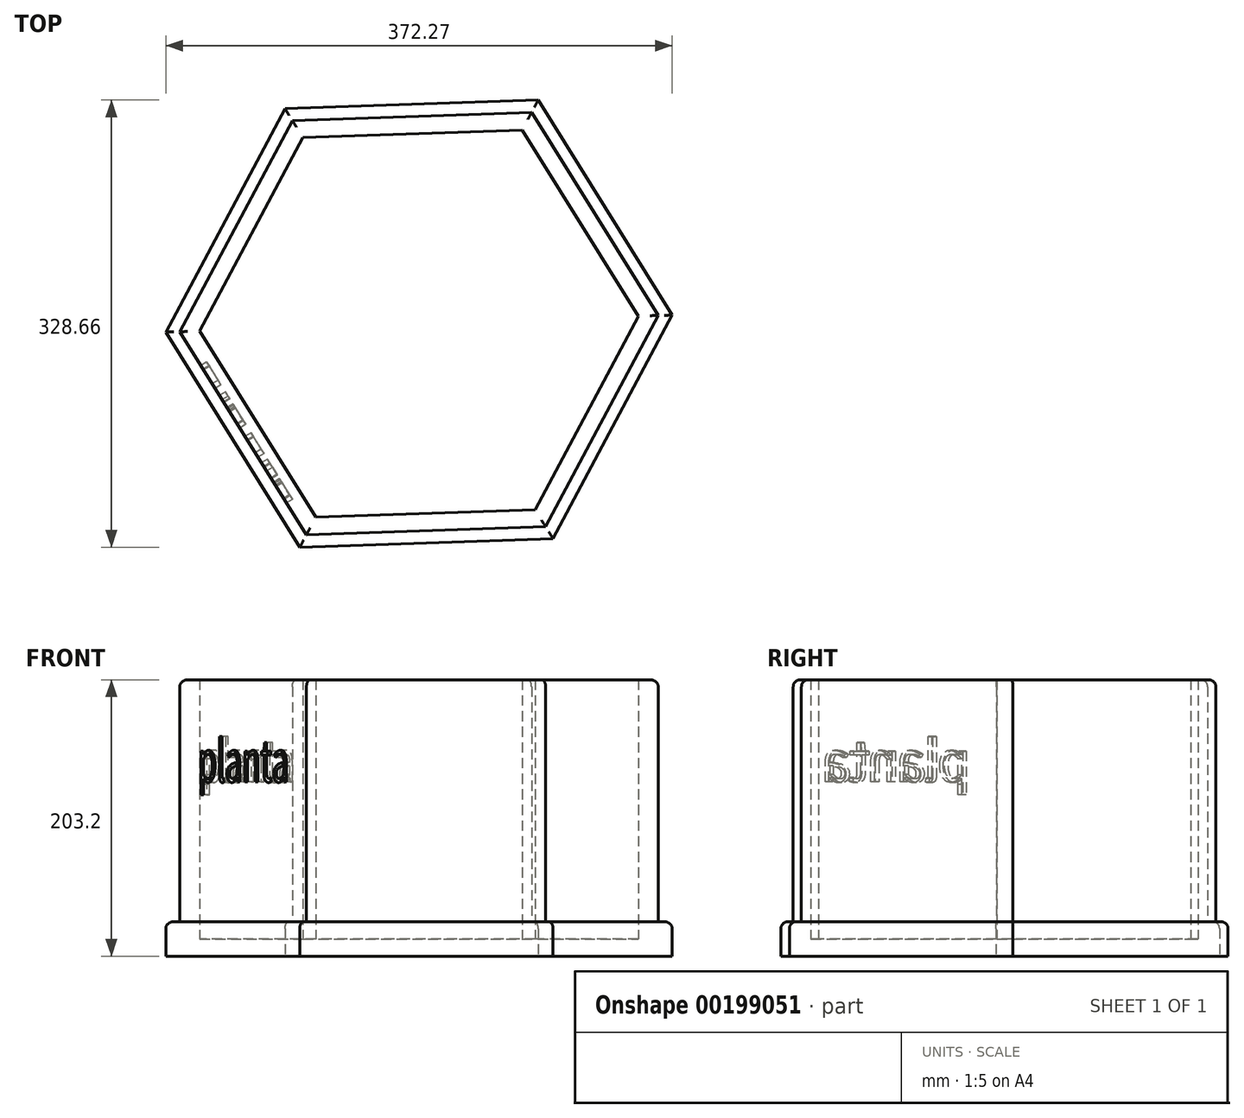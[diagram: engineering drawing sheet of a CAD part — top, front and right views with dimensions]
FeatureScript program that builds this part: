
annotation { "Feature Type Name" : "Feature", "Feature Type Description" : "" }
export const myFeature = defineFeature(function(context is Context, id is Id, definition is map)
    precondition{}
    {
        {
            var Q0;
            Q0=qCreatedBy(makeId("Top.planeOp"),FACE);
            var sketch = newSketch(context, id + "F0", { "sketchPlane" : qUnion([Q0])});
            skCircle(sketch, "E0.cCircle", {"center": v(-49.02, 41.52) * mm, "radius": 152.4 * mm, "construction": true});
            skLineSegment(sketch, "E0.0", {"start": v(126.85, 47.53) * mm, "end": v(44.12, -107.79) * mm});
            skLineSegment(sketch, "E0.1", {"start": v(44.12, -107.79) * mm, "end": v(-131.76, -113.8) * mm});
            skLineSegment(sketch, "E0.2", {"start": v(-131.76, -113.8) * mm, "end": v(-224.9, 35.51) * mm});
            skLineSegment(sketch, "E0.3", {"start": v(-224.9, 35.51) * mm, "end": v(-142.16, 190.83) * mm});
            skLineSegment(sketch, "E0.4", {"start": v(-142.16, 190.83) * mm, "end": v(33.71, 196.84) * mm});
            skLineSegment(sketch, "E0.5", {"start": v(33.71, 196.84) * mm, "end": v(126.85, 47.53) * mm});
            skPoint(sketch, "E0.0.midPoint", {"position": v(85.48, -30.13) * mm});
            skCircle(sketch, "E1.cCircle", {"center": v(-49.02, 41.52) * mm, "radius": 161.3 * mm, "construction": true});
            skLineSegment(sketch, "E1.0", {"start": v(137.11, 47.79) * mm, "end": v(49.47, -116.54) * mm});
            skLineSegment(sketch, "E1.1", {"start": v(49.47, -116.54) * mm, "end": v(-136.66, -122.81) * mm});
            skLineSegment(sketch, "E1.2", {"start": v(-136.66, -122.81) * mm, "end": v(-235.16, 35.25) * mm});
            skLineSegment(sketch, "E1.3", {"start": v(-235.16, 35.25) * mm, "end": v(-147.52, 199.59) * mm});
            skLineSegment(sketch, "E1.4", {"start": v(-147.52, 199.59) * mm, "end": v(38.62, 205.85) * mm});
            skLineSegment(sketch, "E1.5", {"start": v(38.62, 205.85) * mm, "end": v(137.11, 47.79) * mm});
            skPoint(sketch, "E1.0.midPoint", {"position": v(93.3, -34.38) * mm});
            skSolve(sketch);
        }
        {
            var Q0;
            Q0=makeQuery(id+"F0.imprint","IMPRINT",FACE,{"disambiguationData":[TD([[makeQuery(id+"F0.imprint","IMPRINT",EDGE,{"derivedFrom":sQuery(id+"F0.wireOp",EDGE,"E0.0")}),-1.0]])]});
            extrude(context, id + "F1", {"entities" : qUnion([Q0]), "depth" : 203.2 * mm});
        }
        {
            var Q0;
            Q0 = qSketchRegion(id + "F0", true);
            extrude(context, id + "F2", {"entities" : qUnion([Q0]), "operationType" : NewBodyOperationType.ADD, "depth" : 25.4 * mm});
        }
        {
            var Q0;
            Q0=makeQuery(id+"F1.opExtrude","CAP_FACE",FACE,{"disambiguationData":[OSD([sQuery(id+"F0.wireOp",EDGE,"E0.0"),sQuery(id+"F0.wireOp",EDGE,"E0.1"),sQuery(id+"F0.wireOp",EDGE,"E0.2"),sQuery(id+"F0.wireOp",EDGE,"E0.3"),sQuery(id+"F0.wireOp",EDGE,"E0.4"),sQuery(id+"F0.wireOp",EDGE,"E0.5")])],"isStart":false});
            shell(context, id + "F3", {"entities" : qUnion([Q0]), "thickness" : 12.7 * mm});
        }
        {
            var Q0;
            Q0=makeQuery(id+"F2.opExtrude","CAP_EDGE",EDGE,{"disambiguationData":[OSD([sQuery(id+"F0.wireOp",EDGE,"E1.2")])],"isStart":false});
            var Q1;
            Q1=makeQuery(id+"F2.opExtrude","CAP_EDGE",EDGE,{"disambiguationData":[OSD([sQuery(id+"F0.wireOp",EDGE,"E1.1")])],"isStart":false});
            var Q2;
            Q2=makeQuery(id+"F2.opExtrude","CAP_EDGE",EDGE,{"disambiguationData":[OSD([sQuery(id+"F0.wireOp",EDGE,"E1.0")])],"isStart":false});
            var Q3;
            Q3=makeQuery(id+"F2.opExtrude","CAP_EDGE",EDGE,{"disambiguationData":[OSD([sQuery(id+"F0.wireOp",EDGE,"E1.3")])],"isStart":false});
            var Q4;
            Q4=makeQuery(id+"F2.opExtrude","CAP_EDGE",EDGE,{"disambiguationData":[OSD([sQuery(id+"F0.wireOp",EDGE,"E1.4")])],"isStart":false});
            var Q5;
            Q5=makeQuery(id+"F2.opExtrude","CAP_EDGE",EDGE,{"disambiguationData":[OSD([sQuery(id+"F0.wireOp",EDGE,"E1.5")])],"isStart":false});
            fillet(context, id + "F4", {"entities" : qUnion([Q0, Q1, Q2, Q3, Q4, Q5]), "radius" : 5.08 * mm, "tangentPropagation" : true, "allowEdgeOverflow" : false});
        }
        {
            var Q0;
            Q0=makeQuery(id+"F1.opExtrude","SWEPT_FACE",FACE,{"disambiguationData":[OSD([sQuery(id+"F0.wireOp",EDGE,"E0.2")])]});
            var sketch = newSketch(context, id + "F5", { "sketchPlane" : qUnion([Q0])});
            skText(sketch, "E2", { "text": "planta", "fontName": "NotoSansCJKjp-Regular.otf"});
            const initialGuessF5  = {"E2": [-0.12376, 0.12814, 1, 0, 0.03008]};
            skSetInitialGuess(sketch, initialGuessF5);
            skSolve(sketch);
        }
        {
            var Q0;
            Q0 = qSketchRegion(id + "F5", true);
            extrude(context, id + "F6", {"entities" : qUnion([Q0]), "operationType" : NewBodyOperationType.REMOVE, "oppositeDirection" : true, "depth" : 5.08 * mm});
        }
        {
            var Q0;
            Q0=makeQuery(id+"F1.opExtrude","CAP_EDGE",EDGE,{"disambiguationData":[OSD([sQuery(id+"F0.wireOp",EDGE,"E0.2")])],"isStart":false});
            var Q1;
            Q1=makeQuery(id+"F1.opExtrude","CAP_EDGE",EDGE,{"disambiguationData":[OSD([sQuery(id+"F0.wireOp",EDGE,"E0.1")])],"isStart":false});
            var Q2;
            Q2=makeQuery(id+"F1.opExtrude","CAP_EDGE",EDGE,{"disambiguationData":[OSD([sQuery(id+"F0.wireOp",EDGE,"E0.0")])],"isStart":false});
            var Q3;
            Q3=makeQuery(id+"F1.opExtrude","CAP_EDGE",EDGE,{"disambiguationData":[OSD([sQuery(id+"F0.wireOp",EDGE,"E0.5")])],"isStart":false});
            var Q4;
            Q4=makeQuery(id+"F1.opExtrude","CAP_EDGE",EDGE,{"disambiguationData":[OSD([sQuery(id+"F0.wireOp",EDGE,"E0.4")])],"isStart":false});
            var Q5;
            Q5=makeQuery(id+"F1.opExtrude","CAP_EDGE",EDGE,{"disambiguationData":[OSD([sQuery(id+"F0.wireOp",EDGE,"E0.3")])],"isStart":false});
            fillet(context, id + "F7", {"entities" : qUnion([Q0, Q1, Q2, Q3, Q4, Q5]), "radius" : 5.08 * mm, "tangentPropagation" : true, "allowEdgeOverflow" : false});
        }
    });
